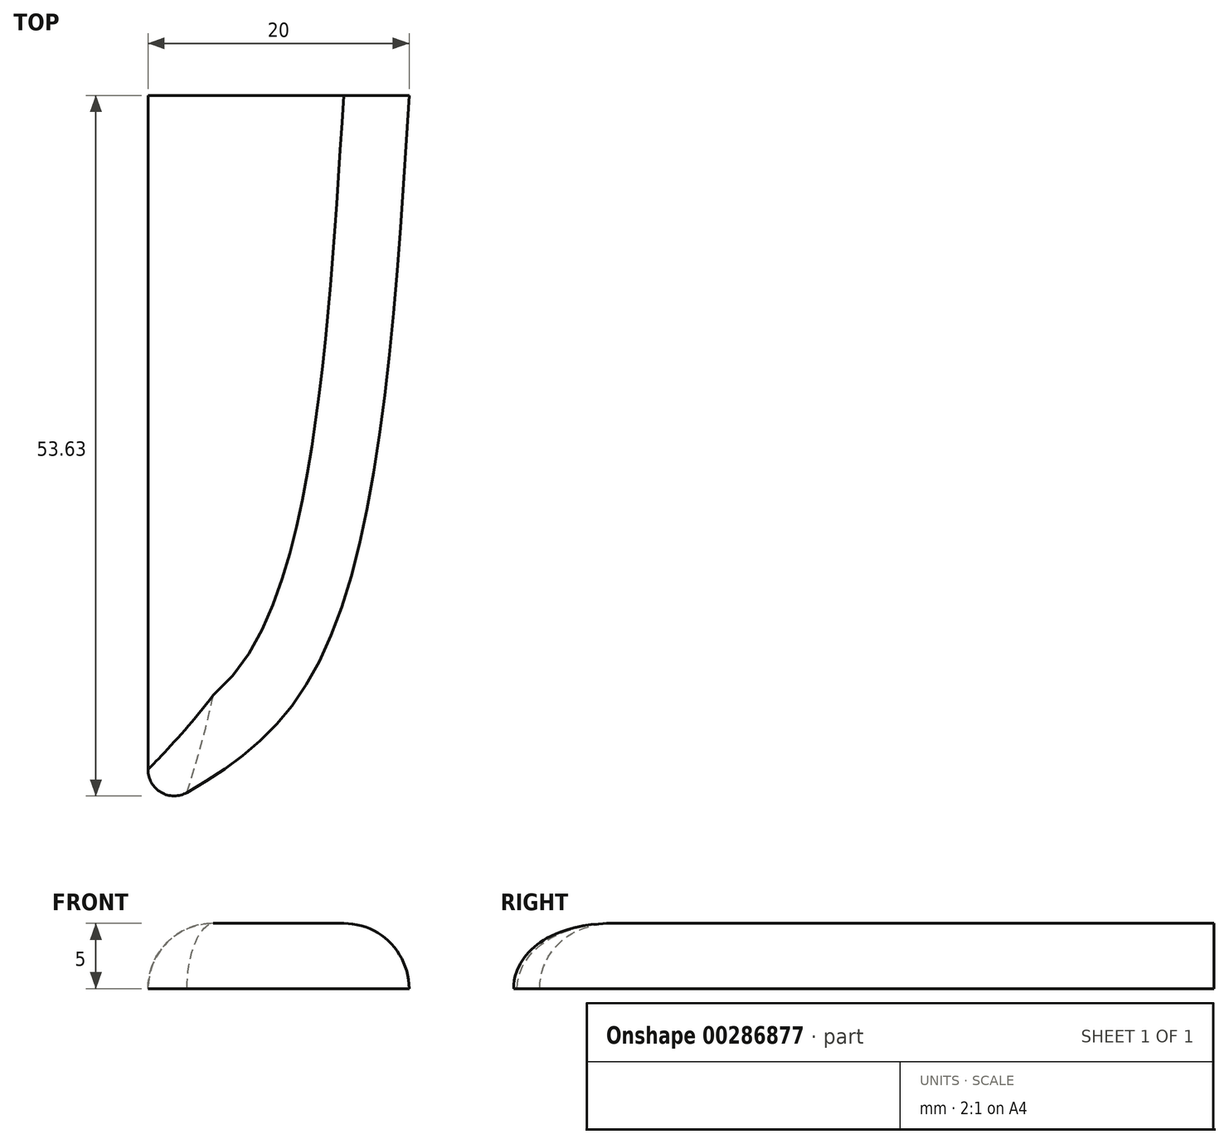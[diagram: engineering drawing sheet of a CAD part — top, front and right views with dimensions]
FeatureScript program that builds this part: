
annotation { "Feature Type Name" : "Feature", "Feature Type Description" : "" }
export const myFeature = defineFeature(function(context is Context, id is Id, definition is map)
    precondition{}
    {
        {
            var Q0;
            Q0=qCreatedBy(makeId("Top.planeOp"),FACE);
            var sketch = newSketch(context, id + "F0", { "sketchPlane" : qUnion([Q0])});
            skLineSegment(sketch, "E0", {"start": v(0, 0) * mm, "end": v(20, 0) * mm});
            skLineSegment(sketch, "E1", {"start": v(0, 0) * mm, "end": v(0, -51.63) * mm});
            skFitSpline(sketch, "E2", {"points": [v(20, 0) * mm, v(12.52, -44.46) * mm, v(0, -55) * mm], "startDerivative": vector(-5.34, -84.72) * mm, "endDerivative": vector(-37.3, -19.92) * mm});
            skArc(sketch, "E3.filletArc", {"start": v(0, -51.63) * mm, "mid": v(1, -53.36) * mm, "end": v(3, -53.36) * mm});
            skSolve(sketch);
        }
        {
            var Q0;
            Q0=makeQuery(id+"F0.imprint","IMPRINT",FACE,{"disambiguationData":[TD([[makeQuery(id+"F0.imprint","IMPRINT",EDGE,{"derivedFrom":sQuery(id+"F0.wireOp",EDGE,"E0")}),-1.0]])]});
            extrude(context, id + "F1", {"entities" : qUnion([Q0]), "depth" : 5 * mm});
        }
        {
            var Q0;
            Q0=makeQuery(id+"F1.opExtrude","CAP_EDGE",EDGE,{"disambiguationData":[OSD([sQuery(id+"F0.wireOp",EDGE,"E2")])],"isStart":false});
            var Q1;
            Q1=makeQuery(id+"F1.opExtrude","CAP_EDGE",EDGE,{"disambiguationData":[OSD([sQuery(id+"F0.wireOp",EDGE,"E3.filletArc")])],"isStart":false});
            var Q2;
            Q2=makeQuery(id+"F1.opExtrude","CAP_EDGE",EDGE,{"disambiguationData":[OSD([sQuery(id+"F0.wireOp",EDGE,"E1")])],"isStart":false});
            fillet(context, id + "F2", {"entities" : qUnion([Q0, Q1, Q2]), "radius" : 5 * mm, "tangentPropagation" : true, "allowEdgeOverflow" : false});
        }
    });
